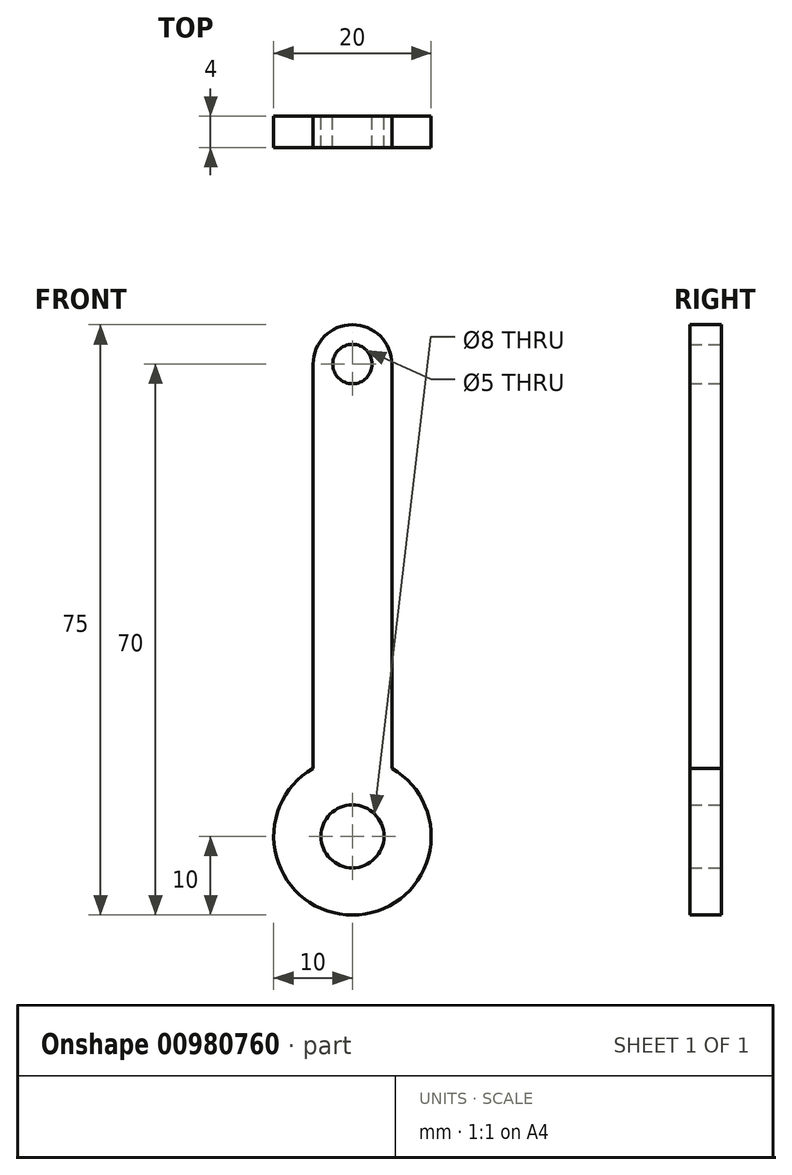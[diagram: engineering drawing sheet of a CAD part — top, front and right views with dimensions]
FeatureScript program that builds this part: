
annotation { "Feature Type Name" : "Feature", "Feature Type Description" : "" }
export const myFeature = defineFeature(function(context is Context, id is Id, definition is map)
    precondition{}
    {
        {
            var Q0;
            Q0=qCreatedBy(makeId("Front.planeOp"),FACE);
            var sketch = newSketch(context, id + "F0", { "sketchPlane" : qUnion([Q0])});
            skArc(sketch, "E0", {"start": v(-5, 8.66) * mm, "mid": v(0, -10) * mm, "end": v(5, 8.66) * mm});
            skCircle(sketch, "E1", {"center": v(0, 0) * mm, "radius": 4 * mm});
            skArc(sketch, "E2", {"start": v(5, 60) * mm, "mid": v(0, 65) * mm, "end": v(-5, 60) * mm});
            skCircle(sketch, "E3", {"center": v(0, 60) * mm, "radius": 2.5 * mm});
            skLineSegment(sketch, "E4", {"start": v(5, 60) * mm, "end": v(5, 8.66) * mm});
            skLineSegment(sketch, "E5", {"start": v(-5, 60) * mm, "end": v(-5, 8.66) * mm});
            skSolve(sketch);
        }
        {
            var Q0;
            Q0=makeQuery(id+"F0.imprint","IMPRINT",FACE,{"disambiguationData":[TD([[makeQuery(id+"F0.imprint","IMPRINT",EDGE,{"derivedFrom":sQuery(id+"F0.wireOp",EDGE,"E0")}),1.0]])]});
            extrude(context, id + "F1", {"entities" : qUnion([Q0]), "depth" : 4 * mm, "offsetDistance" : 25 * mm});
        }
    });
